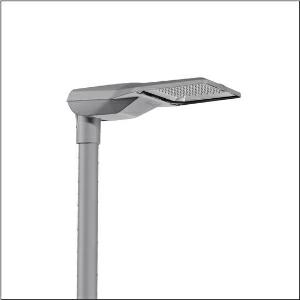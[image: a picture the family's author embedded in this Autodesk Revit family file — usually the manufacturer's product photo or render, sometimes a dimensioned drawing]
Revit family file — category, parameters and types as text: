
# Revit family: streetlight_sl_21_iq_midi___stw1_0a_5xe3e41g08nb_77a4
name_source: partatom
category: Lighting Fixtures
units: mm (PartAtom-declared; Revit-internal decimal feet)

## family parameters
Cut with Voids When Loaded = No
Host = Face
Light Source = No
Part Type = Normal
Room Calculation Point = No
Round Connector Dimension = Use Diameter
Shared = No

## types (1)
- --- (1 x LED, 24250 lm, 155.5 W, 4000K)
    Apparent Load = 155 VA
    CIE Flux Codes = 39 75 98 100 100
    Color Rendering = 70
    Color Temperature = 4000K
    Default Elevation = 1800 mm
    Description = Streetlight SL 21 iQ midi, mast luminaire, primary light control with lens, of PMMA, primary optical cover: cover, of toughened safety glass, transparent, light distribution: STW1.0a, light emission: direct distribution, primary light characteristic: asymmetric, installation type: post-top, side-entry, LED, High Power LED, rated luminous flux: 24.250lm, luminous efficacy: 156lm/W, light colour: 740, colour temperature: 4000K, control: Street-Remote, Auto-Match, Temp-Guard, Lumen-Switch, Night-Set, Smart-Wire, Light-Fading, Desk-Remote (wireless, voltage-free reading and setting of iQ features in the workshop via application-optimized NFC function/RFID function), optimised constant luminous flux control (CLO 2.0), presetting dimming linear, mains connection: 230..240V, AC, 50/60Hz, start of lifetime: 156W, end of service life: 162W, reduction: 69W, luminaire housing, of diecast aluminium, powder-coated, Siteco® metallic grey (DB 702S), corrosivity category C5 mid according to DIN EN ISO 12944, please order mast flange separately, inclination adjustable: 0°, 5°, 10°, 15°, sealing non-destructively replaceable, multi-level sealing system, length: 644mm, width: 335mm, height: 110mm, mast flange for spigot size: 42mm (side-entry): 5XC10008XM4, 60/48mm (side-entry/post-top): 5XC10108XM2, 76/60mm (side-entry/post-top): 5XC10108XM1, protection rating (complete): IP66, insulation class (complete): insulation class II (safety insulation), certification: CE, ENEC, ENEC+, VDE, impact resistance: IK09, permissible operating ambient temperature for outdoor applications: -40..+50°C, standard-compliant lighting for roads and squares, packaging unit: 1 piece

Light Distribution: STW1.0a
    Height = 111 mm
    Lamp = 1 x LED
    Lamp Light Flux = 24250 lm
    Lamp Power = 155.5 W
    Lamp count = 1
    Length = 644 mm
    Luminous efficacy = 156 lm/W
    Manufacturer = Siteco
    ModVariant = No
    Model = 5XE3E41G08NB
    Number of Poles = 1
    OnlyDefault = Yes
    Power Factor = 1
    Product Name = Streetlight SL 21 iQ midi | STW1.0a
    Product group = mast luminaire | pylon top
    ProductGroupID = 6100
    Protection Class = Protection class II
    Protection Degree = IP 66
    RLX_Detail_Level = 1
    RLX_Emergency_Light_Flux = 0 lm
    RLX_Emergency_Type = 0
    RLX_Emergency_Type_DB = No
    RlxData = <blob elided: 92149 chars, md5=1806f265>
    Socket = socket
    Standby Power = 0 W
    System Light Flux = 24250 lm
    System Power = 155 W
    Type Comments = factory setting: luminous flux: 100 % | dim-lin: 254 | 823 mA
    Type Image = l_1004298.jpg
    URL = http://relux.com
    VarID = @adj_102385
    Voltage = 0 V
    Weight = 0.00 kg
    Width = 336 mm

## geometry (parser evidence)
native form markers: Blend x4, Sweep x12
no freeform markers — native parametric forms only
